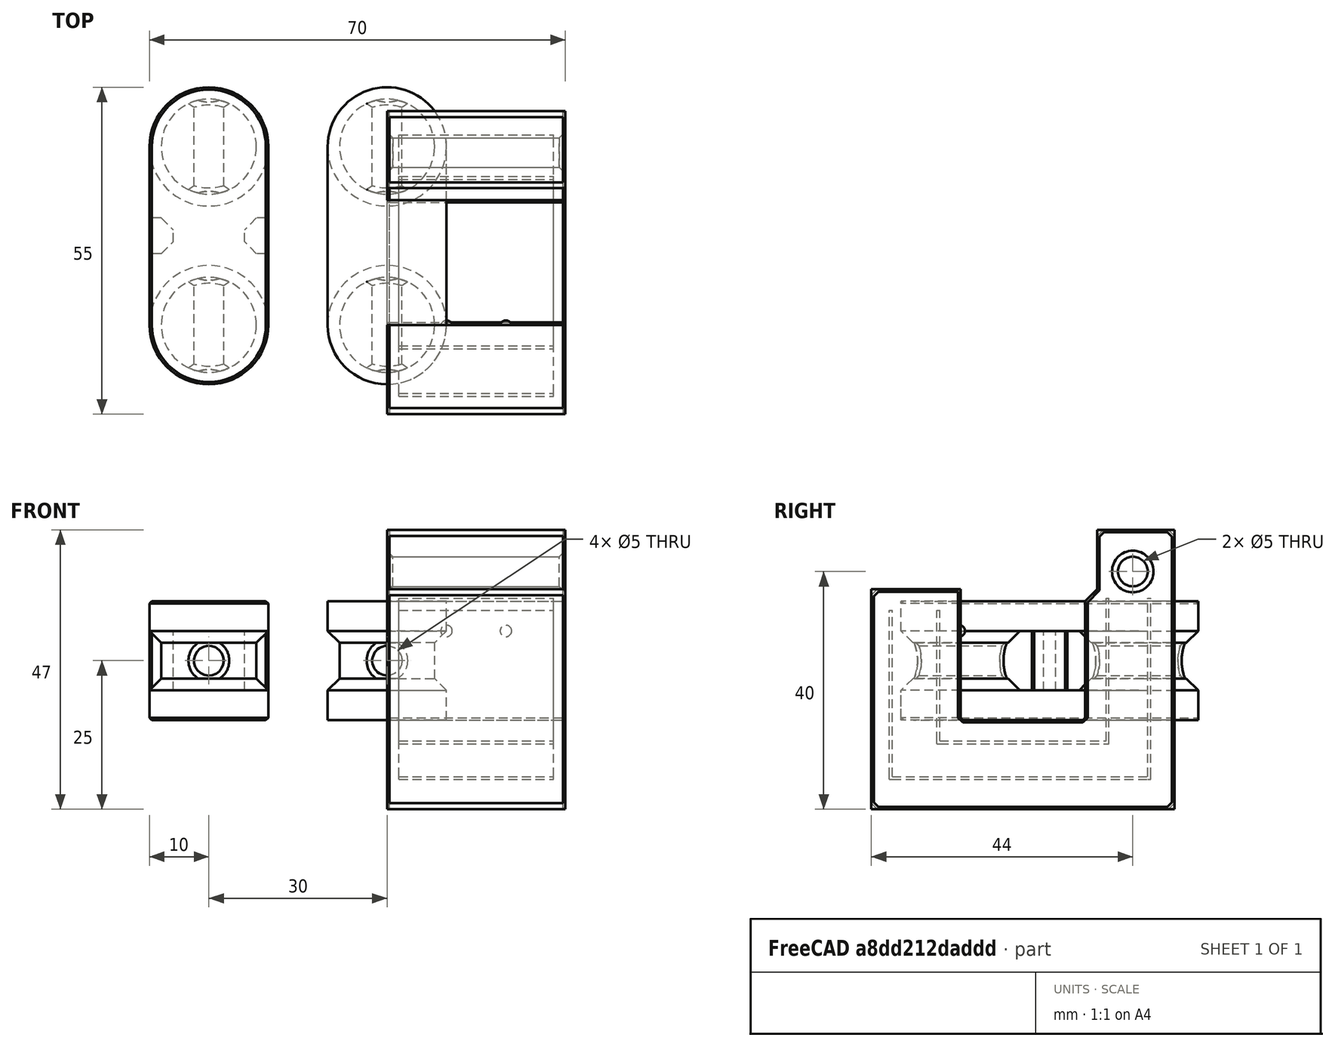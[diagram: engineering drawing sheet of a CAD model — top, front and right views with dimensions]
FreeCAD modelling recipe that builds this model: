
FCSTD DOCUMENT  (FreeCAD 0.18R16146 (Git))
Label: tv-lead
License: All rights reserved
LicenseURL: http://en.wikipedia.org/wiki/All_rights_reserved
objects: Part::Box×13, Part::Chamfer×11, Part::MultiFuse×11, Part::Cylinder×8, Part::Cut×4, Part::Sphere×2, Part::Feature×2
note: 51 computed .brp shape members not serialized (recipe doc carries the construction recipe); baked Part::Feature solids carry a one-line shape summary decoded from their .brp

FEATURE [Part::Box] Box  label="Cube"
  AttacherType = Attacher::AttachEngine3D
  Height = 22
  Length = 30
  Width = 21
FEATURE [Part::Box] Box001  label="Cube001"
  AttacherType = Attacher::AttachEngine3D
  Height = 37
  Length = 30
  Placement = pos=(0,-15,-15) rot=(0,0,1;0rad)
  Width = 51
FEATURE [Part::Cut] Cut
  Base = -> Box001
  Tool = -> Box
FEATURE [Part::Box] Box002  label="Cube002"
  AttacherType = Attacher::AttachEngine3D
  Height = 10
  Length = 30
  Placement = pos=(0,23,22) rot=(0,0,1;0rad)
  Width = 13
FEATURE [Part::Chamfer] Chamfer
  Base = -> Cut
  Edges = 1 edges r=2: [Edge17]
FEATURE [Part::Cylinder] Cylinder
  Angle = 360
  AttacherType = Attacher::AttachEngine3D
  Height = 30
  Placement = pos=(-5.6e-15,29,25) rot=(0,1,0;1.5708rad)
  Radius = 2.5
FEATURE [Part::Cut] Cut001
  Base = -> Box002
  Tool = -> Cylinder
FEATURE [Part::MultiFuse] Fusion
  Shapes = -> [Chamfer,Cut001]
FEATURE [Part::Sphere] Sphere
  Angle1 = -90
  Angle2 = 90
  Angle3 = 360
  AttacherType = Attacher::AttachEngine3D
  Placement = pos=(10,-0.25,15) rot=(0,0,1;0rad)
  Radius = 1
FEATURE [Part::Sphere] Sphere001
  Angle1 = -90
  Angle2 = 90
  Angle3 = 360
  AttacherType = Attacher::AttachEngine3D
  Placement = pos=(20,-0.25,15) rot=(0,0,1;0rad)
  Radius = 1
FEATURE [Part::MultiFuse] Fusion001
  Shapes = -> [Fusion,Sphere001,Sphere]
FEATURE [Part::Feature] Fusion001001  label="Fusion002"
  shape: bbox 30 x 51 x 47 mm, 15 faces (baked)
FEATURE [Part::Chamfer] Chamfer001
  Base = -> Fusion001001
  Edges = 7 edges r=1: [Edge2,Edge4,Edge6,Edge26,Edge29,Edge32,Edge34]
FEATURE [Part::Chamfer] Chamfer002
  Base = -> Chamfer001
  Edges = 32 edges r=0.4: [Edge1,Edge4,Edge5,Edge6,Edge7,Edge8,Edge9,Edge10,Edge11,Edge12,Edge13,Edge14,Edge15,Edge16,Edge17,Edge18,Edge21,Edge23,Edge24,Edge25,Edge26,Edge27,Edge28,Edge29,Edge30,Edge31,Edge32,Edge33,Edge34,Edge35,Edge42,Edge44]
FEATURE [Part::Box] Box003  label="Cube003"
  AttacherType = Attacher::AttachEngine3D
  Height = 0.5
  Length = 26
  Placement = pos=(2,-12,-10) rot=(0,0,1;0rad)
  Width = 44
FEATURE [Part::Box] Box004  label="Cube004"
  AttacherType = Attacher::AttachEngine3D
  Height = 0.5
  Length = 26
  Placement = pos=(2,-4,-4) rot=(0,0,1;0rad)
  Width = 29
FEATURE [Part::Box] Box005  label="Cube005"
  AttacherType = Attacher::AttachEngine3D
  Height = 28.5
  Length = 26
  Placement = pos=(2,-12,-10) rot=(0,0,1;0rad)
  Width = 0.5
FEATURE [Part::Box] Box006  label="Cube006"
  AttacherType = Attacher::AttachEngine3D
  Height = 30.5
  Length = 26
  Placement = pos=(2,31.5,-10) rot=(0,0,1;0rad)
  Width = 0.5
FEATURE [Part::MultiFuse] Fusion001002
  Shapes = -> [Box006,Box005,Box003]
FEATURE [Part::Box] Box007  label="Cube007"
  AttacherType = Attacher::AttachEngine3D
  Height = 22.5
  Length = 26
  Placement = pos=(2,-4,-4) rot=(0,0,1;0rad)
  Width = 0.5
FEATURE [Part::Box] Box008  label="Cube008"
  AttacherType = Attacher::AttachEngine3D
  Height = 24.5
  Length = 26
  Placement = pos=(2,24.5,-4) rot=(0,0,1;0rad)
  Width = 0.5
FEATURE [Part::MultiFuse] Fusion001003
  Shapes = -> [Box008,Box007,Box004]
FEATURE [Part::MultiFuse] Fusion001004
  Shapes = -> [Fusion001003,Fusion001002]
FEATURE [Part::Cut] Cut002  label="bottom-end"
  Base = -> Chamfer002
  Tool = -> Fusion001004
FEATURE [Part::Cylinder] Cylinder001
  Angle = 360
  AttacherType = Attacher::AttachEngine3D
  Height = 7
  Radius = 10
FEATURE [Part::Cylinder] Cylinder002
  Angle = 360
  AttacherType = Attacher::AttachEngine3D
  Height = 7
  Placement = pos=(0,30,0) rot=(0,0,1;0rad)
  Radius = 10
FEATURE [Part::Box] Box009  label="Cube009"
  AttacherType = Attacher::AttachEngine3D
  Height = 5
  Length = 20
  Placement = pos=(-10,0,0) rot=(0,0,1;0rad)
  Width = 30
FEATURE [Part::Box] Box010  label="Cube010"
  AttacherType = Attacher::AttachEngine3D
  Height = 5
  Length = 20
  Placement = pos=(-10,0,15) rot=(0,0,1;0rad)
  Width = 30
FEATURE [Part::Cylinder] Cylinder003
  Angle = 360
  AttacherType = Attacher::AttachEngine3D
  Height = 62
  Placement = pos=(0,-15,10) rot=(1,0,0;4.71239rad)
  Radius = 2.5
FEATURE [Part::Cylinder] Cylinder004
  Angle = 360
  AttacherType = Attacher::AttachEngine3D
  Height = 7
  Placement = pos=(0,30,15) rot=(0,0,1;0rad)
  Radius = 10
FEATURE [Part::Cylinder] Cylinder005
  Angle = 360
  AttacherType = Attacher::AttachEngine3D
  Height = 7
  Placement = pos=(0,0,15) rot=(0,0,1;0rad)
  Radius = 10
FEATURE [Part::Cylinder] Cylinder006
  Angle = 360
  AttacherType = Attacher::AttachEngine3D
  Height = 20
  Placement = pos=(0,30,0) rot=(0,0,1;0rad)
  Radius = 8
FEATURE [Part::Cylinder] Cylinder007
  Angle = 360
  AttacherType = Attacher::AttachEngine3D
  Height = 20
  Radius = 8
FEATURE [Part::MultiFuse] Fusion001005
  Placement = pos=(0,0,-2) rot=(0,0,1;0rad)
  Shapes = -> [Cylinder004,Cylinder005]
FEATURE [Part::MultiFuse] Fusion001006
  Shapes = -> [Cylinder002,Cylinder001]
FEATURE [Part::Chamfer] Chamfer003
  Base = -> Fusion001005
  Edges = 2 edges r=2: [Edge3,Edge6]
FEATURE [Part::Chamfer] Chamfer004
  Base = -> Fusion001006
  Edges = 2 edges r=2: [Edge1,Edge4]
FEATURE [Part::MultiFuse] Fusion001007
  Shapes = -> [Cylinder006,Cylinder007]
FEATURE [Part::Cut] Cut003
  Base = -> Fusion001007
  Tool = -> Cylinder003
FEATURE [Part::Chamfer] Chamfer005
  Base = -> Cut003
  Edges = 4 edges r=1: [Edge4,Edge5,Edge10,Edge11]
FEATURE [Part::MultiFuse] Fusion001008
  Shapes = -> [Chamfer005,Chamfer004,Chamfer003,Box009,Box010]
FEATURE [Part::Feature] Fusion001008001  label="Fusion001009"
  shape: bbox 20 x 50 x 20 mm, 34 faces (baked)
FEATURE [Part::Chamfer] Chamfer006
  Base = -> Fusion001008001
  Edges = 8 edges r=0.4: [Edge4,Edge5,Edge13,Edge20,Edge72,Edge78,Edge81,Edge82]
FEATURE [Part::Box] Box011  label="Cube011"
  AttacherType = Attacher::AttachEngine3D
  Height = 16
  Length = 4
  Placement = pos=(-10,12,2) rot=(0,0,1;0rad)
  Width = 6
FEATURE [Part::Box] Box012  label="Cube012"
  AttacherType = Attacher::AttachEngine3D
  Height = 16
  Length = 4
  Placement = pos=(6,12,2) rot=(0,0,1;0rad)
  Width = 6
FEATURE [Part::Chamfer] Chamfer007
  Base = -> Box011
  Edges = 2 edges r=2: [Edge5,Edge7]
FEATURE [Part::Chamfer] Chamfer008
  Base = -> Box012
  Edges = 2 edges r=2: [Edge1,Edge3]
FEATURE [Part::Chamfer] Chamfer009
  Base = -> Chamfer007
  Edges = 2 edges r=0.4: [Edge17,Edge18]
FEATURE [Part::Chamfer] Chamfer010
  Base = -> Chamfer008
  Edges = 2 edges r=0.4: [Edge17,Edge18]
FEATURE [Part::MultiFuse] Fusion001008002
  Shapes = -> [Chamfer009,Chamfer010]
FEATURE [Part::MultiFuse] Fusion001008003  label="node"
  Placement = pos=(-30,0,0) rot=(0,0,1;0rad)
  Shapes = -> [Chamfer006,Fusion001008002]
